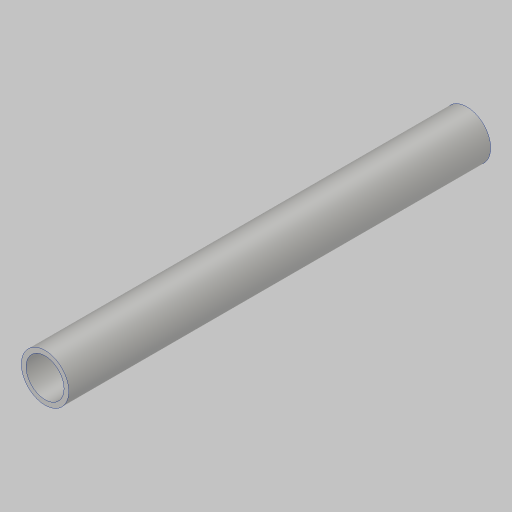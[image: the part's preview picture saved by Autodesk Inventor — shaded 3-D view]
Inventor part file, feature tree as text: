
AUTODESK INVENTOR PART (.ipt)
format: ipt  version: 2023.5 (Build 275446000, 446)  size: 171,008 bytes
history: native  units: in
note: dims shown in document units (in); Inventor stores cm internally (conversion verified against a paired STEP export)
features: extrude x1, sketch x1
ambient origin geometry x8: Origin, YZ Plane, XZ Plane, XY Plane, X Axis, Y Axis, Z Axis, Center Point
bodies: Solid1 (feature_tree)
feature tree (2):
  extrude  "Extrusion1"  Depth=11.1175in
  sketch  "Sketch1"  dims[d0=1.25in d1=0.125in d2=11.1175in d3=0.0in]
